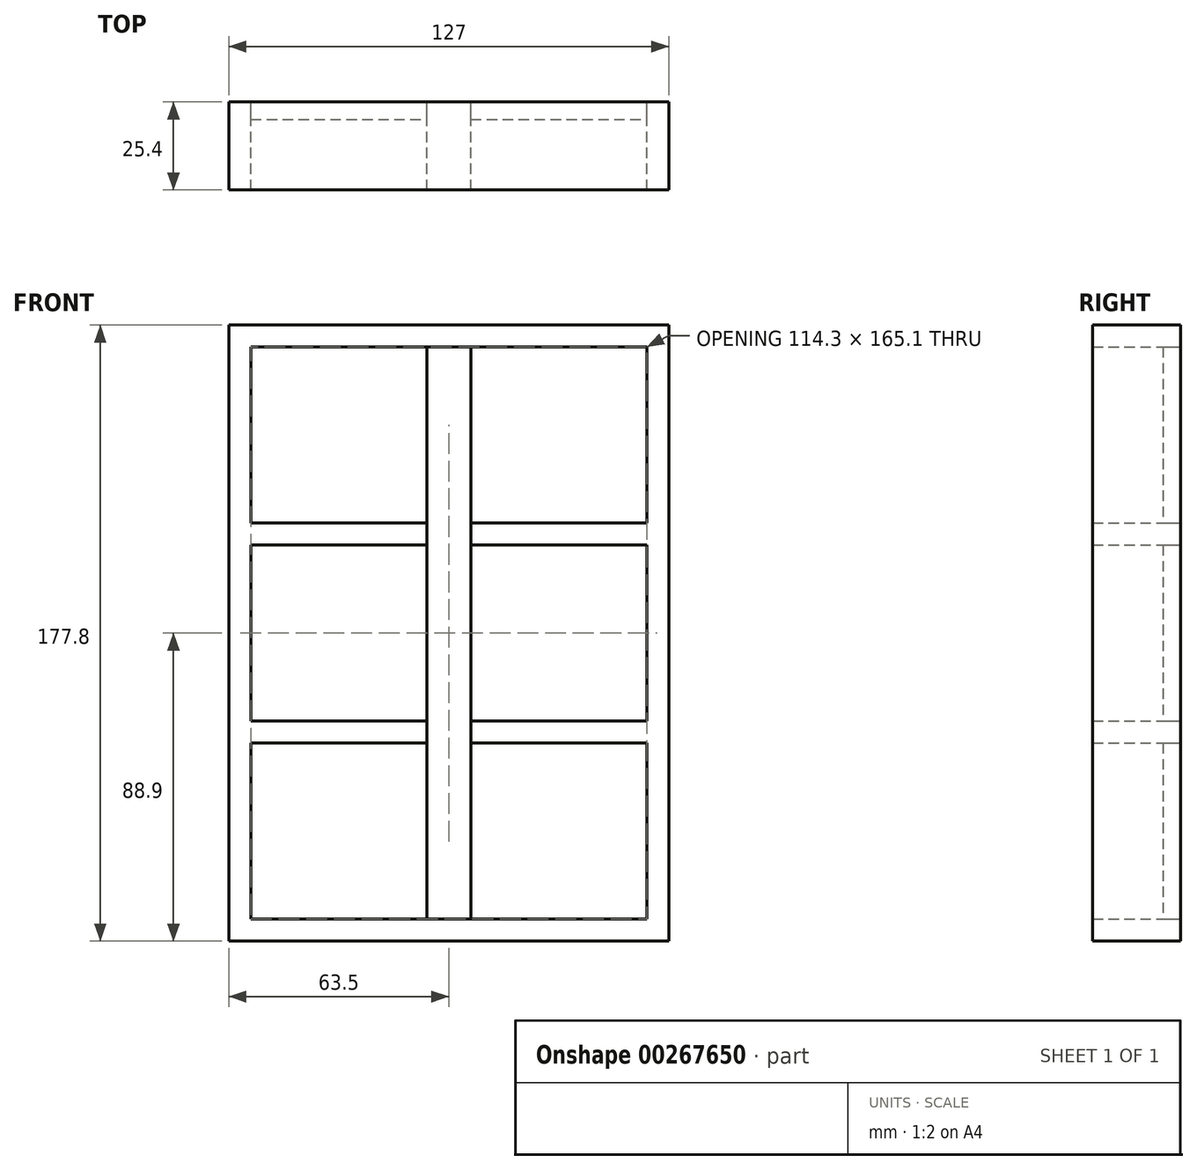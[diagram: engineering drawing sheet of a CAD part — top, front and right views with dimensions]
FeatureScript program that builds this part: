
annotation { "Feature Type Name" : "Feature", "Feature Type Description" : "" }
export const myFeature = defineFeature(function(context is Context, id is Id, definition is map)
    precondition{}
    {
        {
            var Q0;
            Q0=qCreatedBy(makeId("Front.planeOp"),FACE);
            var sketch = newSketch(context, id + "F0", { "sketchPlane" : qUnion([Q0])});
            skLineSegment(sketch, "E0.bottom", {"start": v(63.5, 88.9) * mm, "end": v(-63.5, 88.9) * mm});
            skLineSegment(sketch, "E0.top", {"start": v(63.5, -88.9) * mm, "end": v(-63.5, -88.9) * mm});
            skLineSegment(sketch, "E0.left", {"start": v(63.5, 88.9) * mm, "end": v(63.5, -88.9) * mm});
            skLineSegment(sketch, "E0.right", {"start": v(-63.5, 88.9) * mm, "end": v(-63.5, -88.9) * mm});
            skPoint(sketch, "E0.middle", {"position": v(0, 0) * mm});
            skLineSegment(sketch, "E1.bottom", {"start": v(-57.15, 82.55) * mm, "end": v(57.15, 82.55) * mm});
            skLineSegment(sketch, "E1.top", {"start": v(-57.15, -82.55) * mm, "end": v(57.15, -82.55) * mm});
            skLineSegment(sketch, "E1.left", {"start": v(-57.15, 82.55) * mm, "end": v(-57.15, -82.55) * mm});
            skLineSegment(sketch, "E1.right", {"start": v(57.15, 82.55) * mm, "end": v(57.15, -82.55) * mm});
            skLineSegment(sketch, "E2.bottom", {"start": v(-6.35, 82.55) * mm, "end": v(6.35, 82.55) * mm});
            skLineSegment(sketch, "E2.top", {"start": v(-6.35, -82.55) * mm, "end": v(6.35, -82.55) * mm});
            skLineSegment(sketch, "E2.left", {"start": v(-6.35, 82.55) * mm, "end": v(-6.35, -82.55) * mm});
            skLineSegment(sketch, "E2.right", {"start": v(6.35, 82.55) * mm, "end": v(6.35, -82.55) * mm});
            skLineSegment(sketch, "E3.bottom", {"start": v(-57.15, 82.55) * mm, "end": v(-6.35, 82.55) * mm});
            skLineSegment(sketch, "E3.top", {"start": v(-57.15, 31.75) * mm, "end": v(-6.35, 31.75) * mm});
            skLineSegment(sketch, "E3.left", {"start": v(-57.15, 82.55) * mm, "end": v(-57.15, 31.75) * mm});
            skLineSegment(sketch, "E3.right", {"start": v(-6.35, 82.55) * mm, "end": v(-6.35, 31.75) * mm});
            skLineSegment(sketch, "E4.top", {"start": v(-57.15, 25.4) * mm, "end": v(-6.35, 25.4) * mm});
            skLineSegment(sketch, "E4.left", {"start": v(-57.15, 31.75) * mm, "end": v(-57.15, 25.4) * mm});
            skLineSegment(sketch, "E4.right", {"start": v(-6.35, 31.75) * mm, "end": v(-6.35, 25.4) * mm});
            skLineSegment(sketch, "E5.top", {"start": v(-57.15, -25.4) * mm, "end": v(-6.35, -25.4) * mm});
            skLineSegment(sketch, "E5.left", {"start": v(-57.15, 25.4) * mm, "end": v(-57.15, -25.4) * mm});
            skLineSegment(sketch, "E5.right", {"start": v(-6.35, 25.4) * mm, "end": v(-6.35, -25.4) * mm});
            skLineSegment(sketch, "E6.top", {"start": v(-57.15, -31.75) * mm, "end": v(-6.35, -31.75) * mm});
            skLineSegment(sketch, "E6.left", {"start": v(-57.15, -25.4) * mm, "end": v(-57.15, -31.75) * mm});
            skLineSegment(sketch, "E6.right", {"start": v(-6.35, -25.4) * mm, "end": v(-6.35, -31.75) * mm});
            skLineSegment(sketch, "E7.top", {"start": v(-57.15, -82.55) * mm, "end": v(-6.35, -82.55) * mm});
            skLineSegment(sketch, "E7.left", {"start": v(-57.15, -31.75) * mm, "end": v(-57.15, -82.55) * mm});
            skLineSegment(sketch, "E7.right", {"start": v(-6.35, -31.75) * mm, "end": v(-6.35, -82.55) * mm});
            skLineSegment(sketch, "E8.MirrorCS", {"start": v(57.15, 31.75) * mm, "end": v(6.35, 31.75) * mm});
            skLineSegment(sketch, "E9.MirrorCS", {"start": v(57.15, 25.4) * mm, "end": v(6.35, 25.4) * mm});
            skLineSegment(sketch, "E10.MirrorCS", {"start": v(57.15, -25.4) * mm, "end": v(6.35, -25.4) * mm});
            skLineSegment(sketch, "E11.MirrorCS", {"start": v(57.15, -31.75) * mm, "end": v(6.35, -31.75) * mm});
            skSolve(sketch);
        }
        {
            var Q0;
            Q0=makeQuery(id+"F0.imprint","IMPRINT",FACE,{"disambiguationData":[TD([[makeQuery(id+"F0.imprint","IMPRINT",EDGE,{"derivedFrom":sQuery(id+"F0.wireOp",EDGE,"E0.bottom")}),1.0]])]});
            var Q1;
            Q1=makeQuery(id+"F0.imprint","IMPRINT",FACE,{"disambiguationData":[TD([[makeQuery(id+"F0.imprint","IMPRINT",EDGE,{"derivedFrom":sQuery(id+"F0.wireOp",EDGE,"E3.top")}),-1.0]])]});
            var Q2;
            {var subQ0=sQuery(id+"F0.wireOp",EDGE,"E8.MirrorCS");Q2=makeQuery(id+"F0.imprint","IMPRINT",FACE,{"disambiguationData":[TD([[makeQuery(id+"F0.imprint","IMPRINT",EDGE,{"derivedFrom":subQ0}),1.0]])]});}
            var Q3;
            {var subQ1=sQuery(id+"F0.wireOp",EDGE,"E2.bottom");Q3=makeQuery(id+"F0.imprint","IMPRINT",FACE,{"disambiguationData":[TD([[makeQuery(id+"F0.imprint","IMPRINT",EDGE,{"derivedFrom":subQ1}),-1.0]])]});}
            var Q4;
            {var subQ0=sQuery(id+"F0.wireOp",EDGE,"E10.MirrorCS");Q4=makeQuery(id+"F0.imprint","IMPRINT",FACE,{"disambiguationData":[TD([[makeQuery(id+"F0.imprint","IMPRINT",EDGE,{"derivedFrom":subQ0}),1.0]])]});}
            var Q5;
            Q5=makeQuery(id+"F0.imprint","IMPRINT",FACE,{"disambiguationData":[TD([[makeQuery(id+"F0.imprint","IMPRINT",EDGE,{"derivedFrom":sQuery(id+"F0.wireOp",EDGE,"E5.top")}),-1.0]])]});
            extrude(context, id + "F1", {"entities" : qUnion([Q0, Q1, Q2, Q3, Q4, Q5]), "depth" : 25.4 * mm});
        }
        {
            var Q0;
            Q0=makeQuery(id+"F0.imprint","IMPRINT",FACE,{"disambiguationData":[TD([[makeQuery(id+"F0.imprint","IMPRINT",EDGE,{"derivedFrom":sQuery(id+"F0.wireOp",EDGE,"E3.bottom")}),-1.0]])]});
            var Q1;
            {var subQ0=sQuery(id+"F0.wireOp",EDGE,"E1.bottom");Q1=makeQuery(id+"F0.imprint","IMPRINT",FACE,{"disambiguationData":[TD([[makeQuery(id+"F0.imprint","IMPRINT",EDGE,{"derivedFrom":subQ0}),-1.0]])]});}
            var Q2;
            {var subQ0=sQuery(id+"F0.wireOp",EDGE,"E9.MirrorCS");Q2=makeQuery(id+"F0.imprint","IMPRINT",FACE,{"disambiguationData":[TD([[makeQuery(id+"F0.imprint","IMPRINT",EDGE,{"derivedFrom":subQ0}),1.0]])]});}
            var Q3;
            Q3=makeQuery(id+"F0.imprint","IMPRINT",FACE,{"disambiguationData":[TD([[makeQuery(id+"F0.imprint","IMPRINT",EDGE,{"derivedFrom":sQuery(id+"F0.wireOp",EDGE,"E4.top")}),-1.0]])]});
            var Q4;
            Q4=makeQuery(id+"F0.imprint","IMPRINT",FACE,{"disambiguationData":[TD([[makeQuery(id+"F0.imprint","IMPRINT",EDGE,{"derivedFrom":sQuery(id+"F0.wireOp",EDGE,"E6.top")}),-1.0]])]});
            var Q5;
            {var subQ0=sQuery(id+"F0.wireOp",EDGE,"E1.top");Q5=makeQuery(id+"F0.imprint","IMPRINT",FACE,{"disambiguationData":[TD([[makeQuery(id+"F0.imprint","IMPRINT",EDGE,{"derivedFrom":subQ0}),1.0]])]});}
            extrude(context, id + "F2", {"entities" : qUnion([Q0, Q1, Q2, Q3, Q4, Q5]), "depth" : 5.08 * mm});
        }
    });
